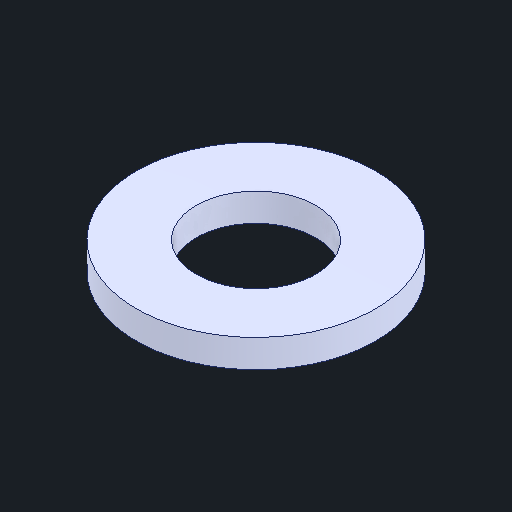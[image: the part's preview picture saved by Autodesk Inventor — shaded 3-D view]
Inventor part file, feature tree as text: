
AUTODESK INVENTOR PART (.ipt)
format: ipt  version: 2025 (Build 290162000, 162)  size: 87,552 bytes
history: native  units: in
note: dims shown in document units (in); Inventor stores cm internally (conversion verified against a paired STEP export)
features: extrude x1
ambient origin geometry x8: Origin, YZ Plane, XZ Plane, XY Plane, X Axis, Y Axis, Z Axis, Center Point
bodies: Solid1 (feature_tree)
feature tree (1):
  extrude  "Extrude1"  [1 undecoded]
note: 1 required parameter value undecoded (feature->parameter linkage not recoverable at this tier; creation-order binding heuristic only, values carry confidence <= 0.55)
